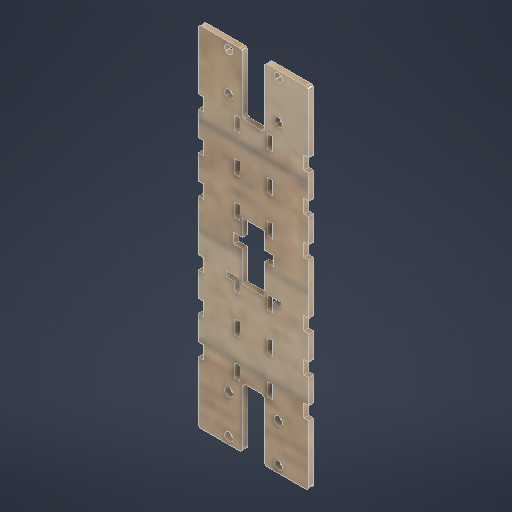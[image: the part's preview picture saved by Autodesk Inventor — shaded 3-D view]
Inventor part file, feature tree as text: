
AUTODESK INVENTOR PART (.ipt)
format: ipt  version: 2025.3 (Build 293356030, 356C)  size: 489,472 bytes
history: native  units: mm
features: sketch x3, other x2, extrude x2
ambient origin geometry x8: Origin, YZ Plane, XZ Plane, XY Plane, X Axis, Y Axis, Z Axis, Center Point
bodies: Body1 (feature_tree)
feature tree (7):
  other  "實體1"
  extrude  "擠出1"  Depth=66.0mm
  sketch  "草圖3"
  extrude  "擠出3"  Depth=208.0mm
  sketch  "草圖1"
  other  "草圖 - 矩形陣列1"
  sketch  "草圖4"
